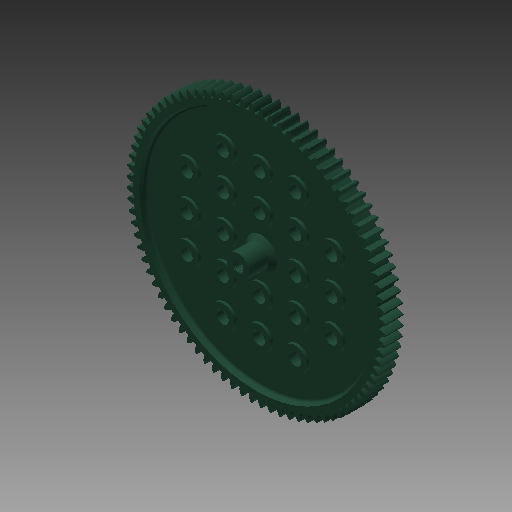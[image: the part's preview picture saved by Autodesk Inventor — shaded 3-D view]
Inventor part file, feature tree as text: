
AUTODESK INVENTOR PART (.ipt)
format: ipt  version: 2018 (Build 220112000, 112)  size: 1,203,200 bytes
history: native  units: mm (DEFAULTED — no unit token found)
features: imported_body x1, sketch x1, other x1, extrude x1
ambient origin geometry x8: Origin, YZ Plane, XZ Plane, XY Plane, X Axis, Y Axis, Z Axis, Center Point
bodies: Solid1 (feature_tree)
feature tree (4):
  imported_body  "Base1"
  sketch  "Sketch1"  dims[d1=8.001mm d5=25.4mm d6=0.0mm d7=0.0mm d8=0.0mm]
  other  "Srf1"
  extrude  "ExtrusionSrf1"  Depth=25.4mm TaperAngle=0.0deg
